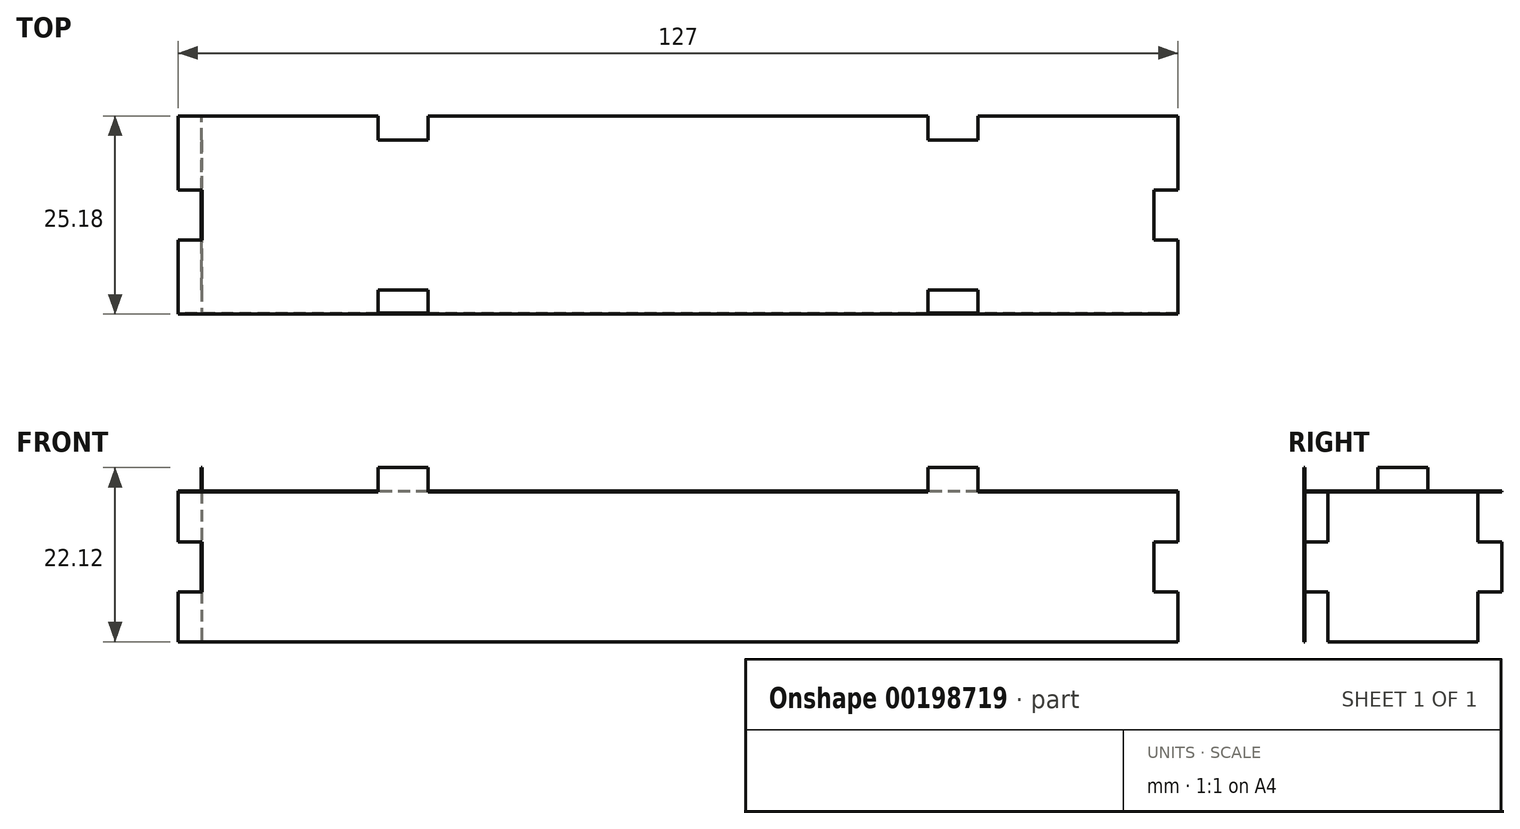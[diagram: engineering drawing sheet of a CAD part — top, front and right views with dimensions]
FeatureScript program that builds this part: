
annotation { "Feature Type Name" : "Feature", "Feature Type Description" : "" }
export const myFeature = defineFeature(function(context is Context, id is Id, definition is map)
    precondition{}
    {
        {
            assignVariable(context, id + "F0", {"name" : "H", "anyValue" : .121});
        }
        {
            var Q0;
            Q0=qCreatedBy(makeId("Front.planeOp"),FACE);
            var sketch = newSketch(context, id + "F1", { "sketchPlane" : qUnion([Q0])});
            skLineSegment(sketch, "E0", {"start": v(0, 0) * mm, "end": v(127, 0) * mm});
            skLineSegment(sketch, "E1", {"start": v(127, 0) * mm, "end": v(127, 6.35) * mm});
            skLineSegment(sketch, "E2", {"start": v(127, 6.35) * mm, "end": v(123.93, 6.35) * mm});
            skLineSegment(sketch, "E3", {"start": v(123.93, 6.35) * mm, "end": v(123.93, 12.7) * mm});
            skLineSegment(sketch, "E4", {"start": v(123.93, 12.7) * mm, "end": v(127, 12.7) * mm});
            skLineSegment(sketch, "E5", {"start": v(127, 12.7) * mm, "end": v(127, 19.05) * mm});
            skLineSegment(sketch, "E6", {"start": v(127, 19.05) * mm, "end": v(101.6, 19.05) * mm});
            skLineSegment(sketch, "E7", {"start": v(101.6, 19.05) * mm, "end": v(101.6, 22.12) * mm});
            skLineSegment(sketch, "E8", {"start": v(101.6, 22.12) * mm, "end": v(95.25, 22.12) * mm});
            skLineSegment(sketch, "E9", {"start": v(95.25, 22.12) * mm, "end": v(95.25, 19.05) * mm});
            skLineSegment(sketch, "E10", {"start": v(95.25, 19.05) * mm, "end": v(31.75, 19.05) * mm});
            skLineSegment(sketch, "E11", {"start": v(31.75, 19.05) * mm, "end": v(31.75, 22.12) * mm});
            skLineSegment(sketch, "E12", {"start": v(31.75, 22.12) * mm, "end": v(25.4, 22.12) * mm});
            skLineSegment(sketch, "E13", {"start": v(25.4, 22.12) * mm, "end": v(25.4, 19.05) * mm});
            skLineSegment(sketch, "E14", {"start": v(25.4, 19.05) * mm, "end": v(0, 19.05) * mm});
            skLineSegment(sketch, "E15", {"start": v(0, 19.05) * mm, "end": v(0, 12.7) * mm});
            skLineSegment(sketch, "E16", {"start": v(0, 12.7) * mm, "end": v(3.07, 12.7) * mm});
            skLineSegment(sketch, "E17", {"start": v(3.07, 12.7) * mm, "end": v(3.07, 6.35) * mm});
            skLineSegment(sketch, "E18", {"start": v(3.07, 6.35) * mm, "end": v(0, 6.35) * mm});
            skLineSegment(sketch, "E19", {"start": v(0, 6.35) * mm, "end": v(0, 0) * mm});
            skSolve(sketch);
        }
        {
            var Q0;
            Q0=makeQuery(id+"F1.imprint","IMPRINT",FACE,{"disambiguationData":[TD([[makeQuery(id+"F1.imprint","IMPRINT",EDGE,{"derivedFrom":sQuery(id+"F1.wireOp",EDGE,"E0")}),1.0]])]});
            extrude(context, id + "F2", {"entities" : qUnion([Q0]), "oppositeDirection" : true, "depth" : (getVariable(context, 'H')) * mm});
        }
        {
            var Q0;
            Q0=makeQuery(id+"F2.opExtrude","SWEPT_FACE",FACE,{"disambiguationData":[OSD([sQuery(id+"F1.wireOp",EDGE,"E10")])]});
            var sketch = newSketch(context, id + "F3", { "sketchPlane" : qUnion([Q0])});
            skLineSegment(sketch, "E20.0", {"start": v(25.4, 0) * mm, "end": v(0, 0) * mm});
            skLineSegment(sketch, "E21.0", {"start": v(25.4, 3.07) * mm, "end": v(25.4, 0) * mm});
            skLineSegment(sketch, "E22.0", {"start": v(31.75, 3.07) * mm, "end": v(25.4, 3.07) * mm});
            skLineSegment(sketch, "E23.0", {"start": v(31.75, 3.07) * mm, "end": v(31.75, 0) * mm});
            skLineSegment(sketch, "E24.0", {"start": v(95.25, 0) * mm, "end": v(31.75, 0) * mm});
            skLineSegment(sketch, "E25.0", {"start": v(95.25, 3.07) * mm, "end": v(95.25, 0) * mm});
            skLineSegment(sketch, "E26.0", {"start": v(101.6, 3.07) * mm, "end": v(95.25, 3.07) * mm});
            skLineSegment(sketch, "E27.0", {"start": v(101.6, 3.07) * mm, "end": v(101.6, 0) * mm});
            skLineSegment(sketch, "E28.0", {"start": v(127, 0) * mm, "end": v(101.6, 0) * mm});
            skLineSegment(sketch, "E29", {"start": v(0, 0) * mm, "end": v(0, 9.41) * mm});
            skLineSegment(sketch, "E30", {"start": v(0, 9.41) * mm, "end": v(3.07, 9.41) * mm});
            skLineSegment(sketch, "E31", {"start": v(3.07, 9.41) * mm, "end": v(3.07, 15.76) * mm});
            skLineSegment(sketch, "E32", {"start": v(3.07, 15.76) * mm, "end": v(0, 15.76) * mm});
            skLineSegment(sketch, "E33", {"start": v(0, 15.76) * mm, "end": v(0, 25.18) * mm});
            skLineSegment(sketch, "E34", {"start": v(0, 25.18) * mm, "end": v(25.4, 25.18) * mm});
            skLineSegment(sketch, "E35", {"start": v(25.4, 25.18) * mm, "end": v(25.4, 22.1) * mm});
            skLineSegment(sketch, "E36", {"start": v(25.4, 22.1) * mm, "end": v(31.75, 22.1) * mm});
            skLineSegment(sketch, "E37", {"start": v(31.75, 22.1) * mm, "end": v(31.75, 25.18) * mm});
            skLineSegment(sketch, "E38", {"start": v(31.75, 25.18) * mm, "end": v(95.25, 25.18) * mm});
            skLineSegment(sketch, "E39", {"start": v(95.25, 25.18) * mm, "end": v(95.25, 22.1) * mm});
            skLineSegment(sketch, "E40", {"start": v(95.25, 22.1) * mm, "end": v(101.6, 22.1) * mm});
            skLineSegment(sketch, "E41", {"start": v(101.6, 22.1) * mm, "end": v(101.6, 25.18) * mm});
            skLineSegment(sketch, "E42", {"start": v(101.6, 25.18) * mm, "end": v(127, 25.18) * mm});
            skLineSegment(sketch, "E43", {"start": v(127, 25.18) * mm, "end": v(127, 15.76) * mm});
            skLineSegment(sketch, "E44", {"start": v(127, 15.76) * mm, "end": v(123.93, 15.76) * mm});
            skLineSegment(sketch, "E45", {"start": v(123.93, 15.76) * mm, "end": v(123.93, 9.41) * mm});
            skLineSegment(sketch, "E46", {"start": v(123.93, 9.41) * mm, "end": v(127, 9.41) * mm});
            skLineSegment(sketch, "E47", {"start": v(127, 9.41) * mm, "end": v(127, 0) * mm});
            skSolve(sketch);
        }
        {
            var Q0;
            Q0=makeQuery(id+"F3.imprint","IMPRINT",FACE,{"disambiguationData":[TD([[makeQuery(id+"F3.imprint","IMPRINT",EDGE,{"derivedFrom":sQuery(id+"F3.wireOp",EDGE,"E20.0")}),-1.0]])]});
            var Q1;
            Q1=makeQuery(id+"F3.imprint","IMPRINT",FACE,{"disambiguationData":[TD([[makeQuery(id+"F3.imprint","IMPRINT",EDGE,{"derivedFrom":sQuery(id+"F3.wireOp",EDGE,"E23.0")}),1.0]])]});
            extrude(context, id + "F4", {"entities" : qUnion([Q0, Q1]), "depth" : (getVariable(context, 'H')) * mm});
        }
        {
            var Q0;
            Q0=makeQuery(id+"F2.opExtrude","SWEPT_FACE",FACE,{"disambiguationData":[OSD([sQuery(id+"F1.wireOp",EDGE,"E17")])]});
            var sketch = newSketch(context, id + "F5", { "sketchPlane" : qUnion([Q0])});
            skLineSegment(sketch, "E48.0", {"start": v(-3.07, 6.35) * mm, "end": v(-3.07, 0) * mm});
            skLineSegment(sketch, "E49.0", {"start": v(-3.07, 6.35) * mm, "end": v(0, 6.35) * mm});
            skLineSegment(sketch, "E50.0", {"start": v(0, 12.7) * mm, "end": v(0, 6.35) * mm});
            skLineSegment(sketch, "E51.0", {"start": v(-3.07, 12.7) * mm, "end": v(0, 12.7) * mm});
            skLineSegment(sketch, "E52.0", {"start": v(-3.07, 19.05) * mm, "end": v(-3.07, 12.7) * mm});
            skLineSegment(sketch, "E53.0", {"start": v(-3.07, 19.05) * mm, "end": v(-9.41, 19.05) * mm});
            skLineSegment(sketch, "E54.0", {"start": v(-9.41, 22.12) * mm, "end": v(-9.41, 19.05) * mm});
            skLineSegment(sketch, "E55.0", {"start": v(-9.41, 22.12) * mm, "end": v(-15.76, 22.12) * mm});
            skLineSegment(sketch, "E56.0", {"start": v(-15.76, 22.12) * mm, "end": v(-15.76, 19.05) * mm});
            skLineSegment(sketch, "E57", {"start": v(-15.76, 19.05) * mm, "end": v(-22.1, 19.05) * mm});
            skLineSegment(sketch, "E58", {"start": v(-22.1, 19.05) * mm, "end": v(-22.1, 12.7) * mm});
            skLineSegment(sketch, "E59", {"start": v(-22.1, 12.7) * mm, "end": v(-25.18, 12.7) * mm});
            skLineSegment(sketch, "E60", {"start": v(-25.18, 12.7) * mm, "end": v(-25.18, 6.35) * mm});
            skLineSegment(sketch, "E61", {"start": v(-25.18, 6.35) * mm, "end": v(-22.1, 6.35) * mm});
            skLineSegment(sketch, "E62", {"start": v(-22.1, 6.35) * mm, "end": v(-22.1, 0) * mm});
            skLineSegment(sketch, "E63", {"start": v(-22.1, 0) * mm, "end": v(-3.07, 0) * mm});
            skSolve(sketch);
        }
        {
            var Q0;
            Q0=makeQuery(id+"F5.imprint","IMPRINT",FACE,{"disambiguationData":[TD([[makeQuery(id+"F5.imprint","IMPRINT",EDGE,{"derivedFrom":sQuery(id+"F5.wireOp",EDGE,"E48.0")}),-1.0]])]});
            var Q1;
            Q1=makeQuery(id+"F5.imprint","IMPRINT",FACE,{"disambiguationData":[TD([[makeQuery(id+"F5.imprint","IMPRINT",EDGE,{"derivedFrom":sQuery(id+"F5.wireOp",EDGE,"E49.0")}),1.0]])]});
            extrude(context, id + "F6", {"entities" : qUnion([Q0, Q1]), "depth" : (getVariable(context, 'H')) * mm});
        }
    });
